# Revit family: Terminal_Unit-Carnes-AVWE-Single_Duct-Hot_Water-1_Row
name_source: partatom
category: Mechanical Equipment
revit_build: Autodesk Revit MEP 2012 (Build: 20110309_2315(x64)
units: mm (PartAtom-declared; Revit-internal decimal feet)

## types (10) — shared parameters
04 CSI = 23 34 23
95 CSI = 15830
Assembly Code = D3040200
Catalog URL = http://www.carnes.com
Default Elevation = 0"
Description = Single Duct Terminal Units
Flow Rate = 0.0 L/s
IOM Instructions URL = http://www.carnes.com
Manufacturer = CARNES COMPANY
Manufacturer Fax = 608-845-6470
Material = Galvanized Steel
Modeling Numbering System = http://www.carnes.com
OD Connection 1 = OD Connection 1
OD Connection 2 = OD Connection 2
Product Page URL = http://www.carnes.com
Spec Sheet URL = http://www.carnes.com
Subcategory = Air Volume Terminal Units
URL = http://www.carnes.com
Unit = Metal - Carnes - Steel
ecoScorecard Product Page = http://ecoscorecard.com

## per-type parameters (varying)
| type | A | B | C | CFM Range | E | F | G | H | Inlet Height | Inlet Radius | Inlet Width | OD Connection Diameter | OD Connection Radius |
| AVWE05 | 12" | 8" | 23 5/8" | 0-350 (0-165) | 17" | 7 5/8" | 6 1/4" | 3" | 4 7/8" | 2 7/16" | 4 7/8" | 1/2" | 1/4" |
| AVWE06 | 12" | 8" | 23 5/8" | 0-500 (0-236) | 17" | 7 5/8" | 6 1/4" | 3" | 5 7/8" | 2 15/16" | 5 7/8" | 1/2" | 1/4" |
| AVWE07 | 12" | 10" | 23 5/8" | 0-700 (0-330) | 17" | 10 1/8" | 8 3/4" | 3" | 6 7/8" | 3 7/16" | 6 7/8" | 1/2" | 1/4" |
| AVWE08 | 12" | 10" | 23 5/8" | 0-1000 (0-472) | 17" | 10 1/8" | 8 3/4" | 3" | 7 7/8" | 3 15/16" | 7 7/8" | 1/2" | 1/4" |
| AVWE10 | 14" | 12 1/2" | 23 5/8" | 0-1500 (0-708) | 19" | 12 5/8" | 11 1/4" | 3" | 9 7/8" | 4 15/16" | 9 7/8" | 1/2" | 1/4" |
| AVWE12 | 16" | 15" | 23 5/8" | 0-2300 (0-1085) | 21" | 15 1/8" | 13 3/4" | 3 1/2" | 11 7/8" | 5 15/16" | 11 7/8" | 5/8" | 5/16" |
| AVWE14 | 20" | 17 1/2" | 23 5/8" | 0-3100 (0-1463) | 25" | 17 5/8" | 16 1/4" | 3 1/2" | 13 7/8" | 6 15/16" | 13 7/8" | 5/8" | 5/16" |
| AVWE16 | 24" | 18" | 24 5/8" | 0-4200 (0-1982) | 29" | 17 5/8" | 16 1/4" | 3 1/2" | 15 7/8" | 7 15/16" | 15 7/8" | 5/8" | 5/16" |
| AVWE18 | 32" | 17 1/2" | 26 5/8" | 0-5500 (0-2596) | 37" | 17 5/8" | 16 1/4" | 3 1/2" | 15 7/8" | 8 15/16" | 17 7/8" | 5/8" | 5/16" |
| AVWE24 | 32" | 17 1/2" | 26 5/8" | 0-7300 (0-3445) | 37" | 17 5/8" | 16 1/4" | 3 1/2" | 15 7/8" | 11 15/16" | 23 7/8" | 5/8" | 5/16" |

note: column(s) folded — value = type name in every type: Model

## geometry (parser evidence)
native form markers: Blend x4, Sweep x4
no freeform markers — native parametric forms only
